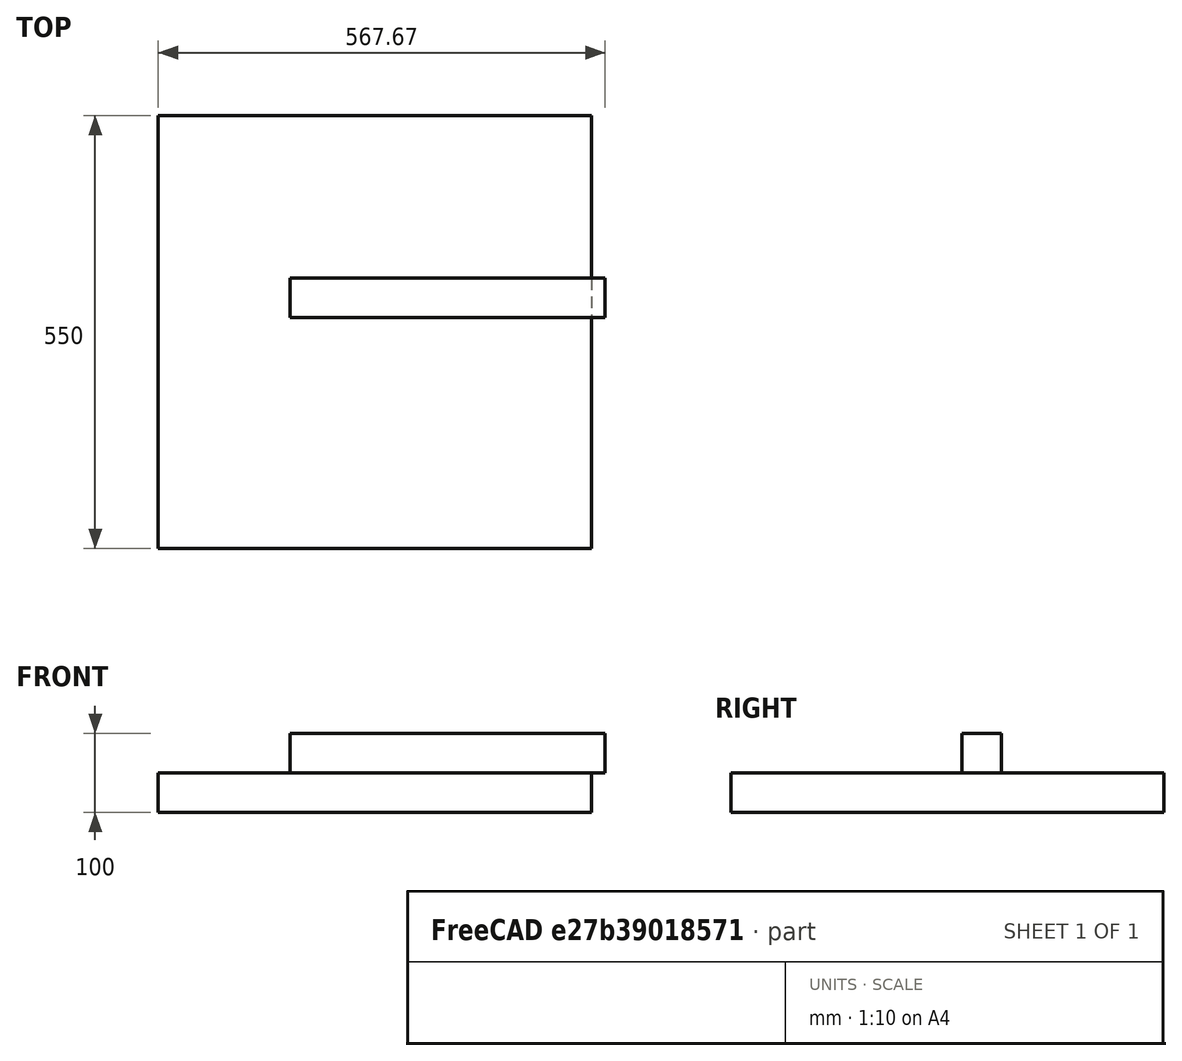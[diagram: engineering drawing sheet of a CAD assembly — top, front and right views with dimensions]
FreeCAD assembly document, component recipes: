
FREECAD ASSEMBLY — COMPONENT RECIPES ("mesa_Ikea")

This assembly document has 5 components, labeled P0..P4 below (a component is one placed body or linked part). 5 of them carry a construction recipe — the FreeCAD feature program that regenerates the part from scratch, quoted from this document or its linked companion documents; the rest are supplied as boundary geometry only. No exploded tour is included for this assembly.
COMPONENT P0 — recipe-attached ("Tablero001", modeled in this document).
Construction recipe (the document's own serialized feature program — sketch geometry with constraints, then the solid features built on it; lengths are millimeters unless a unit is written):

FEATURE [Sketcher::SketchObject] Sketch
  ArcFitTolerance = 1e-06
  AttachmentSupport = -> [YZ_Plane]
  FullyConstrained = false
  MakeInternals = false
  MapMode = 5
  Placement = pos=(0,0,0) rot=(0.57735,0.57735,0.57735;2.0944rad)
  sketch-geometry (4):
    g0: LineSegment StartX=-305.851 StartY=309.369 StartZ=0 EndX=-305.851 EndY=-240.631 EndZ=0
    g1: LineSegment StartX=-305.851 StartY=-240.631 StartZ=0 EndX=244.149 EndY=-240.631 EndZ=0
    g2: LineSegment StartX=244.149 StartY=-240.631 StartZ=0 EndX=244.149 EndY=309.369 EndZ=0
    g3: LineSegment StartX=244.149 StartY=309.369 StartZ=0 EndX=-305.851 EndY=309.369 EndZ=0
  constraints (10):
    c: Coincident(g0,g1)
    c: Coincident(g1,g2)
    c: Coincident(g2,g3)
    c: Coincident(g3,g0)
    c: Vertical(g0)
    c: Vertical(g2)
    c: Horizontal(g1)
    c: Horizontal(g3)
    c: DistanceY(g2,g2) = 550
    c: DistanceX(g1,g1) = 550
FEATURE [PartDesign::Pad] Pad
  Direction = (1,0,0)
  Length = 50
  Length2 = 10
  Placement = pos=(0,0,0) rot=(1,1,1;2.0944rad)
  Profile = -> Sketch
  ReferenceAxis = -> Sketch [N_Axis]
  Refine = true
  Suppressed = false
  Type = 0
FEATURE [PartDesign::Body] Body  label="Boceto tablero"
  AllowCompound = false
  Group = -> [Sketch,Pad]
  Origin = -> Origin001
  Placement = pos=(0,0,0) rot=(0,1,0;1.5708rad)
  Tip = -> Pad
COMPONENT P1 — recipe-attached ("pata001", modeled in this document).
Construction recipe (the document's own serialized feature program — sketch geometry with constraints, then the solid features built on it; lengths are millimeters unless a unit is written):

FEATURE [Sketcher::SketchObject] Sketch003
  ArcFitTolerance = 1e-06
  AttachmentSupport = -> [XY_Plane003]
  FullyConstrained = false
  MakeInternals = false
  MapMode = 5
  sketch-geometry (4):
    g0: LineSegment StartX=-72.9598 StartY=37.5082 StartZ=0 EndX=-72.9598 EndY=-12.4918 EndZ=0
    g1: LineSegment StartX=-72.9598 StartY=-12.4918 StartZ=0 EndX=327.04 EndY=-12.4918 EndZ=0
    g2: LineSegment StartX=327.04 StartY=-12.4918 StartZ=0 EndX=327.04 EndY=37.5082 EndZ=0
    g3: LineSegment StartX=327.04 StartY=37.5082 StartZ=0 EndX=-72.9598 EndY=37.5082 EndZ=0
  constraints (10):
    c: Coincident(g0,g1)
    c: Coincident(g1,g2)
    c: Coincident(g2,g3)
    c: Coincident(g3,g0)
    c: Vertical(g0)
    c: Vertical(g2)
    c: Horizontal(g1)
    c: Horizontal(g3)
    c: Distance(g0,g2) = 400
    c: Distance(g1,g3) = 50
FEATURE [PartDesign::Pad] Pad002
  Direction = (0,0,1)
  Length = 50
  Length2 = 10
  Profile = -> Sketch003
  ReferenceAxis = -> Sketch003 [N_Axis]
  Refine = true
  Suppressed = false
  Type = 0
FEATURE [PartDesign::Body] Body001  label="Body"
  AllowCompound = false
  Group = -> [Sketch003,Pad002]
  Origin = -> Origin003
  Tip = -> Pad002
COMPONENT P2 — same part as P1; its construction recipe is shown at P1.
COMPONENT P3 — same part as P1; its construction recipe is shown at P1.
COMPONENT P4 — same part as P1; its construction recipe is shown at P1.
PROVENANCE & LICENSES
A FreeCAD (.FCStd) document from a public repository crawl; recipes are the document's own serialized feature recipes (and, for linked parts, companion documents' recipes).
License: as declared in the source repository (recorded in the dataset sidecar).
